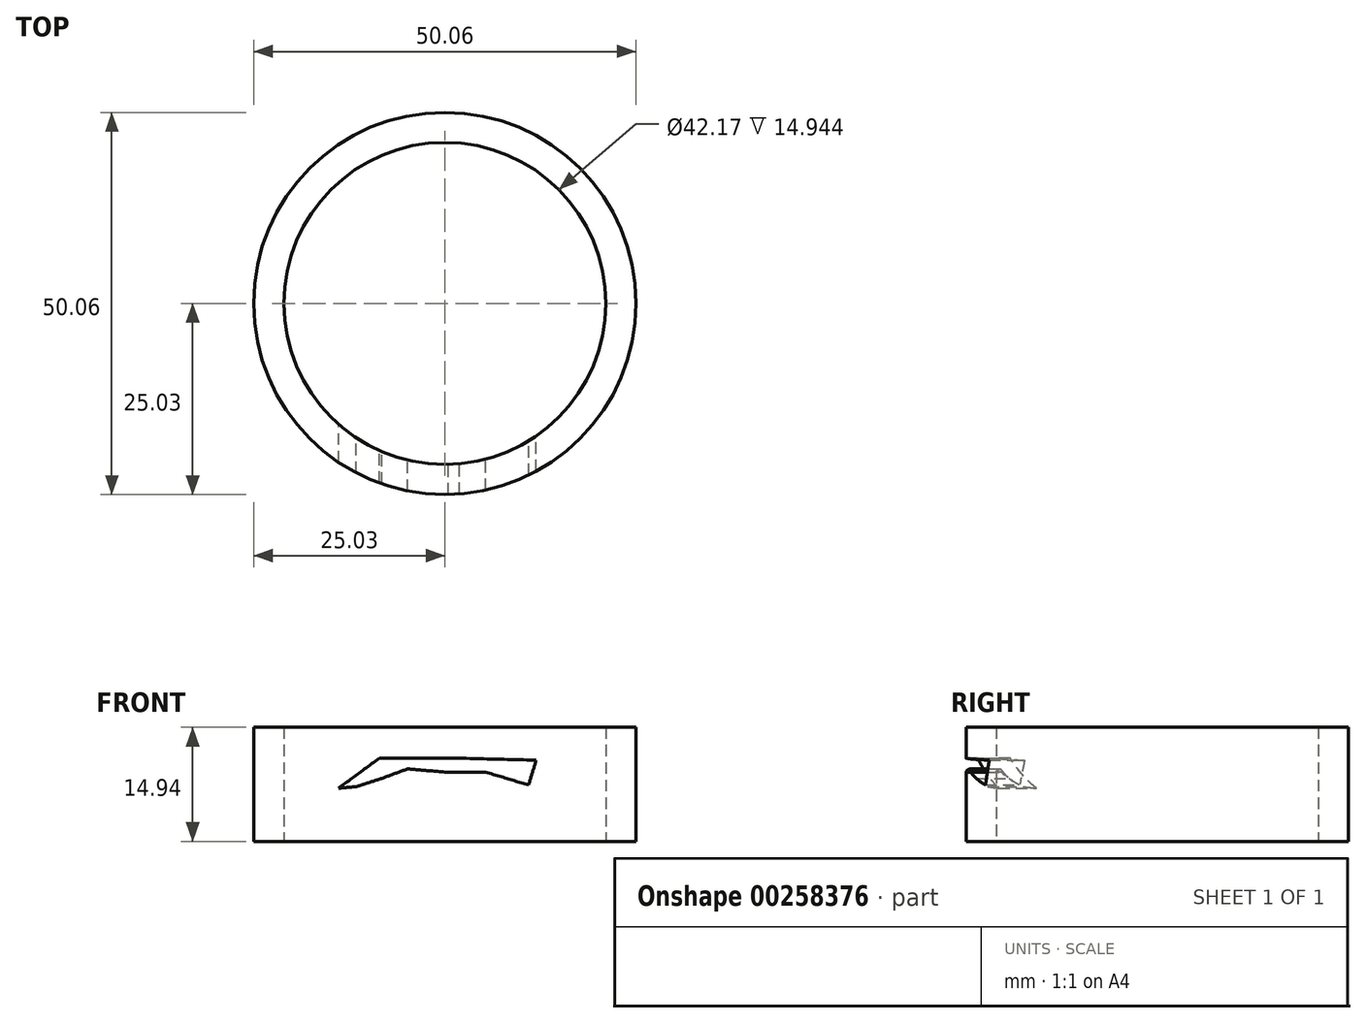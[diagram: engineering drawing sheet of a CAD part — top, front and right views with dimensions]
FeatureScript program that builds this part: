
annotation { "Feature Type Name" : "Feature", "Feature Type Description" : "" }
export const myFeature = defineFeature(function(context is Context, id is Id, definition is map)
    precondition{}
    {
        {
            var Q0;
            Q0=qCreatedBy(makeId("Top.planeOp"),FACE);
            var sketch = newSketch(context, id + "F0", { "sketchPlane" : qUnion([Q0])});
            skCircle(sketch, "E0", {"center": v(0, 0) * mm, "radius": 25.03 * mm});
            skSolve(sketch);
        }
        {
            var Q0;
            Q0=makeQuery(id+"F0.imprint","IMPRINT",FACE,{"disambiguationData":[TD([[makeQuery(id+"F0.imprint","IMPRINT",EDGE,{"derivedFrom":sQuery(id+"F0.wireOp",EDGE,"E0")}),1.0]])]});
            var sketch = newSketch(context, id + "F1", { "sketchPlane" : qUnion([Q0])});
            skCircle(sketch, "E1", {"center": v(0, 0) * mm, "radius": 21.08 * mm});
            skSolve(sketch);
        }
        {
            var Q0;
            Q0=makeQuery(id+"F0.imprint","IMPRINT",FACE,{"disambiguationData":[TD([[makeQuery(id+"F0.imprint","IMPRINT",EDGE,{"derivedFrom":sQuery(id+"F0.wireOp",EDGE,"E0")}),1.0]])]});
            extrude(context, id + "F2", {"entities" : qUnion([Q0]), "depth" : 14.94 * mm});
        }
        {
            var Q0;
            Q0=makeQuery(id+"F1.imprint","IMPRINT",FACE,{"disambiguationData":[TD([[makeQuery(id+"F1.imprint","IMPRINT",EDGE,{"derivedFrom":sQuery(id+"F1.wireOp",EDGE,"E1")}),1.0]])]});
            extrude(context, id + "F3", {"entities" : qUnion([Q0]), "operationType" : NewBodyOperationType.REMOVE, "depth" : 20.7 * mm});
        }
        {
            var Q0;
            Q0=qCreatedBy(makeId("Front.planeOp"),FACE);
            var sketch = newSketch(context, id + "F4", { "sketchPlane" : qUnion([Q0])});
            skLineSegment(sketch, "E2", {"start": v(-13.92, 6.95) * mm, "end": v(-8.6, 10.89) * mm});
            skLineSegment(sketch, "E3", {"start": v(-8.6, 10.89) * mm, "end": v(1.92, 10.89) * mm});
            skLineSegment(sketch, "E4", {"start": v(1.92, 10.89) * mm, "end": v(11.96, 10.63) * mm});
            skLineSegment(sketch, "E5", {"start": v(11.96, 10.63) * mm, "end": v(10.97, 7.37) * mm});
            skLineSegment(sketch, "E6", {"start": v(10.97, 7.37) * mm, "end": v(5.36, 9.06) * mm});
            skLineSegment(sketch, "E7", {"start": v(5.36, 9.06) * mm, "end": v(0.47, 9.02) * mm});
            skLineSegment(sketch, "E8", {"start": v(0.47, 9.02) * mm, "end": v(-4.87, 9.5) * mm});
            skLineSegment(sketch, "E9", {"start": v(-4.87, 9.5) * mm, "end": v(-8.23, 8.25) * mm});
            skLineSegment(sketch, "E10", {"start": v(-8.23, 8.25) * mm, "end": v(-11.6, 7.16) * mm});
            skLineSegment(sketch, "E11", {"start": v(-11.6, 7.16) * mm, "end": v(-13.92, 6.95) * mm});
            skSolve(sketch);
        }
        {
            var Q0;
            Q0=makeQuery(id+"F4.imprint","IMPRINT",FACE,{"disambiguationData":[TD([[makeQuery(id+"F4.imprint","IMPRINT",EDGE,{"derivedFrom":sQuery(id+"F4.wireOp",EDGE,"E2")}),-1.0]])]});
            extrude(context, id + "F5", {"entities" : qUnion([Q0]), "operationType" : NewBodyOperationType.REMOVE, "depth" : 25.4 * mm, "offsetDistance" : 25.4 * mm});
        }
    });
